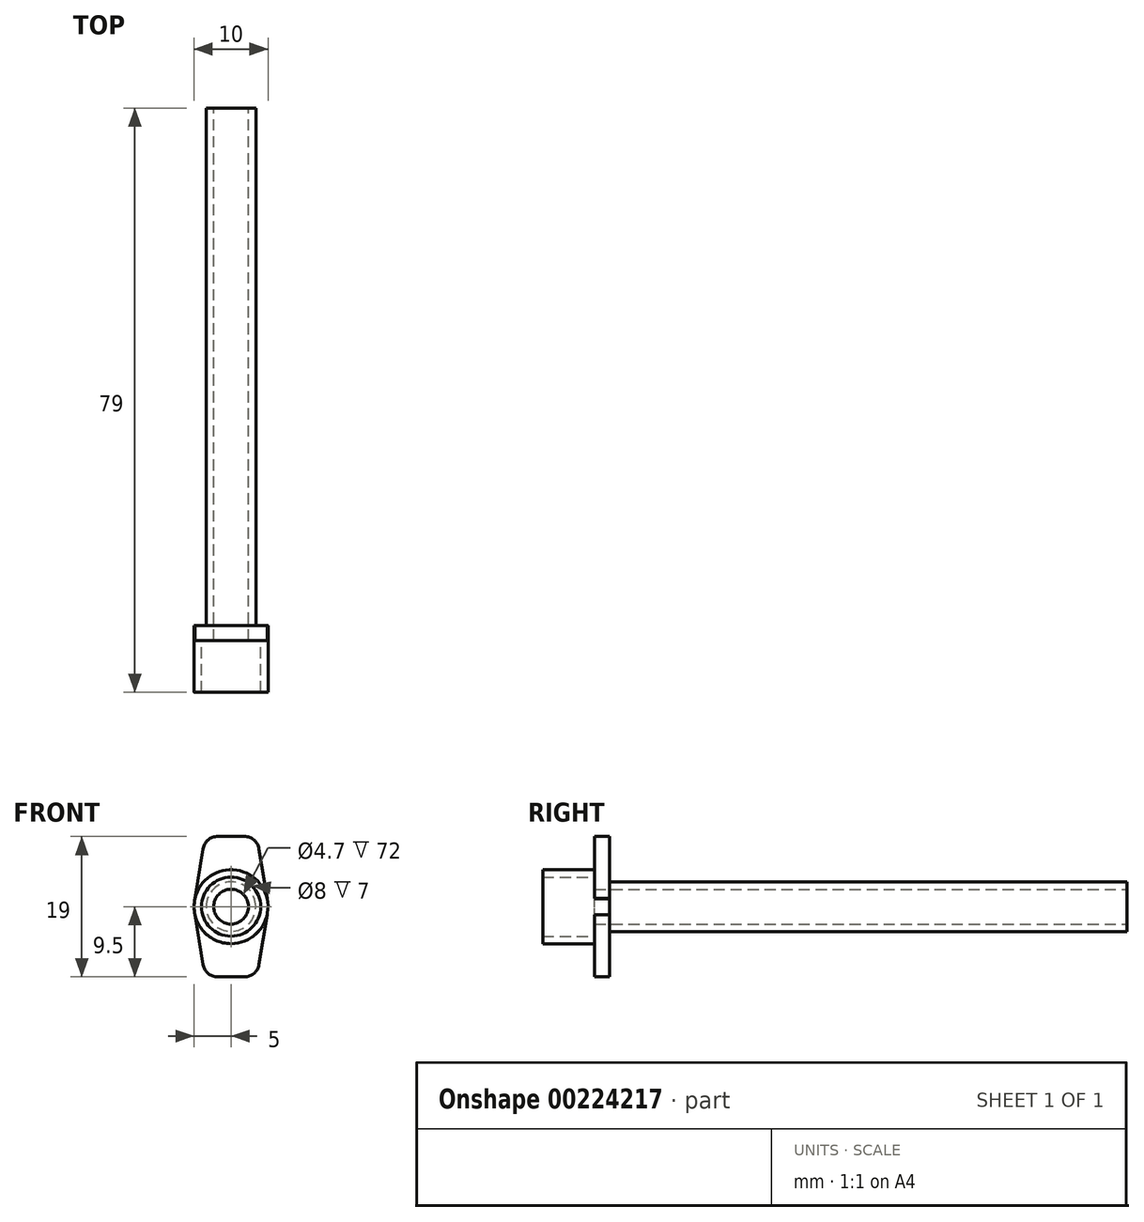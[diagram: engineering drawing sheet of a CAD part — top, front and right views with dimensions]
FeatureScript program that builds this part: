
annotation { "Feature Type Name" : "Feature", "Feature Type Description" : "" }
export const myFeature = defineFeature(function(context is Context, id is Id, definition is map)
    precondition{}
    {
        {
            var Q0;
            Q0=qCreatedBy(makeId("Front.planeOp"),FACE);
            var sketch = newSketch(context, id + "F0", { "sketchPlane" : qUnion([Q0])});
            skCircle(sketch, "E0", {"center": v(0, 0) * mm, "radius": 3.35 * mm});
            skCircle(sketch, "E1.0", {"center": v(0, 0) * mm, "radius": 2.35 * mm});
            skSolve(sketch);
        }
        {
            var Q0;
            Q0=makeQuery(id+"F0.imprint","IMPRINT",FACE,{"disambiguationData":[TD([[makeQuery(id+"F0.imprint","IMPRINT",EDGE,{"derivedFrom":sQuery(id+"F0.wireOp",EDGE,"E0")}),1.0]])]});
            extrude(context, id + "F1", {"entities" : qUnion([Q0]), "depth" : 70 * mm});
        }
        {
            var Q0;
            Q0=makeQuery(id+"F1.opExtrude","CAP_FACE",FACE,{"disambiguationData":[OSD([sQuery(id+"F0.wireOp",EDGE,"E0"),sQuery(id+"F0.wireOp",EDGE,"E1.0")])],"isStart":false});
            var sketch = newSketch(context, id + "F2", { "sketchPlane" : qUnion([Q0])});
            skLineSegment(sketch, "E2.bottom", {"start": v(4.88, 9.5) * mm, "end": v(-4.88, 9.5) * mm});
            skLineSegment(sketch, "E2.top", {"start": v(4.88, -9.5) * mm, "end": v(-4.88, -9.5) * mm});
            skLineSegment(sketch, "E2.left", {"start": v(4.88, 9.5) * mm, "end": v(4.88, -9.5) * mm});
            skLineSegment(sketch, "E2.right", {"start": v(-4.88, 9.5) * mm, "end": v(-4.88, -9.5) * mm});
            skPoint(sketch, "E2.middle", {"position": v(0, 0) * mm});
            skCircle(sketch, "E3", {"center": v(0, 0) * mm, "radius": 5 * mm});
            skLineSegment(sketch, "E4", {"start": v(-4.93, 0.81) * mm, "end": v(-3.5, 9.5) * mm});
            skLineSegment(sketch, "E5", {"start": v(0, 0) * mm, "end": v(0, 9.5) * mm, "construction": true});
            skLineSegment(sketch, "E6", {"start": v(0, 0) * mm, "end": v(5, 0) * mm, "construction": true});
            skLineSegment(sketch, "E7.MirrorCS", {"start": v(4.93, 0.81) * mm, "end": v(3.5, 9.5) * mm});
            skLineSegment(sketch, "E8.MirrorCS", {"start": v(4.93, -0.81) * mm, "end": v(3.5, -9.5) * mm});
            skLineSegment(sketch, "E9.MirrorCS", {"start": v(-4.93, -0.81) * mm, "end": v(-3.5, -9.5) * mm});
            skCircle(sketch, "E10.0", {"center": v(0, 0) * mm, "radius": 2.35 * mm});
            skSolve(sketch);
        }
        {
            var Q0;
            {var subQ5=sQuery(id+"F2.wireOp",EDGE,"E4");var subQ9=sQuery(id+"F2.wireOp",EDGE,"E2.bottom");var subQ10=makeQuery(id+"F2.imprint","INTERSECT",VERTEX,{"derivedFrom":[subQ9,subQ5]});Q0=makeQuery(id+"F2.imprint","IMPRINT",FACE,{"disambiguationData":[TD([[makeQuery(id+"F2.imprint","IMPRINT",EDGE,{"disambiguationData":[TD([[subQ10,1.0]])],"derivedFrom":subQ9}),1.0]])]});}
            var Q1;
            Q1=makeQuery(id+"F2.imprint","IMPRINT",FACE,{"disambiguationData":[TD([[makeQuery(id+"F2.imprint","IMPRINT",EDGE,{"derivedFrom":makeQuery(id+"F1.opExtrude","CAP_EDGE",EDGE,{"disambiguationData":[OSD([sQuery(id+"F0.wireOp",EDGE,"E0")])],"isStart":false})}),-1.0]])]});
            var Q2;
            {var subQ5=sQuery(id+"F2.wireOp",EDGE,"E8.MirrorCS");var subQ8=sQuery(id+"F2.wireOp",EDGE,"E2.top");var subQ11=makeQuery(id+"F2.imprint","INTERSECT",VERTEX,{"derivedFrom":[subQ8,subQ5]});Q2=makeQuery(id+"F2.imprint","IMPRINT",FACE,{"disambiguationData":[TD([[makeQuery(id+"F2.imprint","IMPRINT",EDGE,{"disambiguationData":[TD([[subQ11,-1.0]])],"derivedFrom":subQ8}),-1.0]])]});}
            var Q3;
            Q3=makeQuery(id+"F2.imprint","IMPRINT",FACE,{"disambiguationData":[TD([[makeQuery(id+"F2.imprint","IMPRINT",EDGE,{"derivedFrom":sQuery(id+"F2.wireOp",EDGE,"E10.0")}),-1.0]])]});
            var Q4;
            {var subQ0=sQuery(id+"F2.wireOp",EDGE,"E3");var subQ1=sQuery(id+"F2.wireOp",EDGE,"E2.right");var subQ2=makeQuery(id+"F2.imprint","INTERSECT",VERTEX,{"disambiguationData":[OD(0.0)],"derivedFrom":[subQ1,subQ0]});Q4=makeQuery(id+"F2.imprint","IMPRINT",FACE,{"disambiguationData":[TD([[makeQuery(id+"F2.imprint","IMPRINT",EDGE,{"disambiguationData":[TD([[subQ2,-1.0]])],"derivedFrom":subQ1}),-1.0]])]});}
            var Q5;
            {var subQ0=sQuery(id+"F2.wireOp",EDGE,"E3");var subQ1=sQuery(id+"F2.wireOp",EDGE,"E2.left");var subQ2=makeQuery(id+"F2.imprint","INTERSECT",VERTEX,{"disambiguationData":[OD(0.0)],"derivedFrom":[subQ1,subQ0]});Q5=makeQuery(id+"F2.imprint","IMPRINT",FACE,{"disambiguationData":[TD([[makeQuery(id+"F2.imprint","IMPRINT",EDGE,{"disambiguationData":[TD([[subQ2,-1.0]])],"derivedFrom":subQ1}),1.0]])]});}
            extrude(context, id + "F3", {"entities" : qUnion([Q0, Q1, Q2, Q3, Q4, Q5]), "operationType" : NewBodyOperationType.ADD, "depth" : 2 * mm});
        }
        {
            var Q0;
            Q0=makeQuery(id+"F3.opExtrude","SWEPT_EDGE",EDGE,{"disambiguationData":[OSD([sQuery(id+"F2.wireOp",EDGE,"E2.bottom"),sQuery(id+"F2.wireOp",EDGE,"E4")])]});
            var Q1;
            Q1=makeQuery(id+"F3.opExtrude","SWEPT_EDGE",EDGE,{"disambiguationData":[OSD([sQuery(id+"F2.wireOp",EDGE,"E2.bottom"),sQuery(id+"F2.wireOp",EDGE,"E7.MirrorCS")])]});
            var Q2;
            Q2=makeQuery(id+"F3.opExtrude","SWEPT_EDGE",EDGE,{"disambiguationData":[OSD([sQuery(id+"F2.wireOp",EDGE,"E2.top"),sQuery(id+"F2.wireOp",EDGE,"E8.MirrorCS")])]});
            var Q3;
            Q3=makeQuery(id+"F3.opExtrude","SWEPT_EDGE",EDGE,{"disambiguationData":[OSD([sQuery(id+"F2.wireOp",EDGE,"E2.top"),sQuery(id+"F2.wireOp",EDGE,"E9.MirrorCS")])]});
            fillet(context, id + "F4", {"entities" : qUnion([Q0, Q1, Q2, Q3]), "radius" : 2 * mm, "tangentPropagation" : true, "allowEdgeOverflow" : false});
        }
        {
            var Q0;
            Q0=makeQuery(id+"F3.opExtrude","CAP_FACE",FACE,{"disambiguationData":[OSD([sQuery(id+"F2.wireOp",EDGE,"E2.bottom"),sQuery(id+"F2.wireOp",EDGE,"E2.top"),sQuery(id+"F2.wireOp",EDGE,"E2.left"),sQuery(id+"F2.wireOp",EDGE,"E2.right"),sQuery(id+"F2.wireOp",EDGE,"E3"),sQuery(id+"F2.wireOp",EDGE,"E4"),sQuery(id+"F2.wireOp",EDGE,"E7.MirrorCS"),sQuery(id+"F2.wireOp",EDGE,"E8.MirrorCS"),sQuery(id+"F2.wireOp",EDGE,"E9.MirrorCS"),sQuery(id+"F2.wireOp",EDGE,"E10.0")])],"isStart":false});
            var sketch = newSketch(context, id + "F5", { "sketchPlane" : qUnion([Q0])});
            skCircle(sketch, "E11", {"center": v(0, 0) * mm, "radius": 5 * mm});
            skCircle(sketch, "E12", {"center": v(0, 0) * mm, "radius": 4 * mm});
            skSolve(sketch);
        }
        {
            var Q0;
            Q0 = qSketchRegion(id + "F5", true);
            extrude(context, id + "F6", {"entities" : qUnion([Q0]), "operationType" : NewBodyOperationType.ADD, "depth" : 7 * mm});
        }
    });
